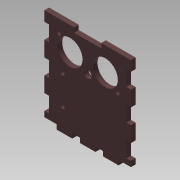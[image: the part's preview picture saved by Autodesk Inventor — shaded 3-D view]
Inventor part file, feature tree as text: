
AUTODESK INVENTOR PART (.ipt)
format: ipt  version: 2015 SP1 (Build 190203100, 203)  size: 152,064 bytes
history: native  units: mm
features: extrude x1, sketch x1
ambient origin geometry x8: Origin, YZ Plane, XZ Plane, XY Plane, X Axis, Y Axis, Z Axis, Center Point
bodies: Solid1 (feature_tree)
feature tree (2):
  extrude  "Extrusion1"  Depth=3.0mm TaperAngle=0.0deg
  sketch  "Sketch1"  dims[d1=20.0mm d3=20.0mm d4=3.0mm d5=15.0mm d6=15.0mm d7=5.0mm d8=10.0mm d9=3.0mm d10=3.0mm d12=3.0mm d13=0.0mm]
